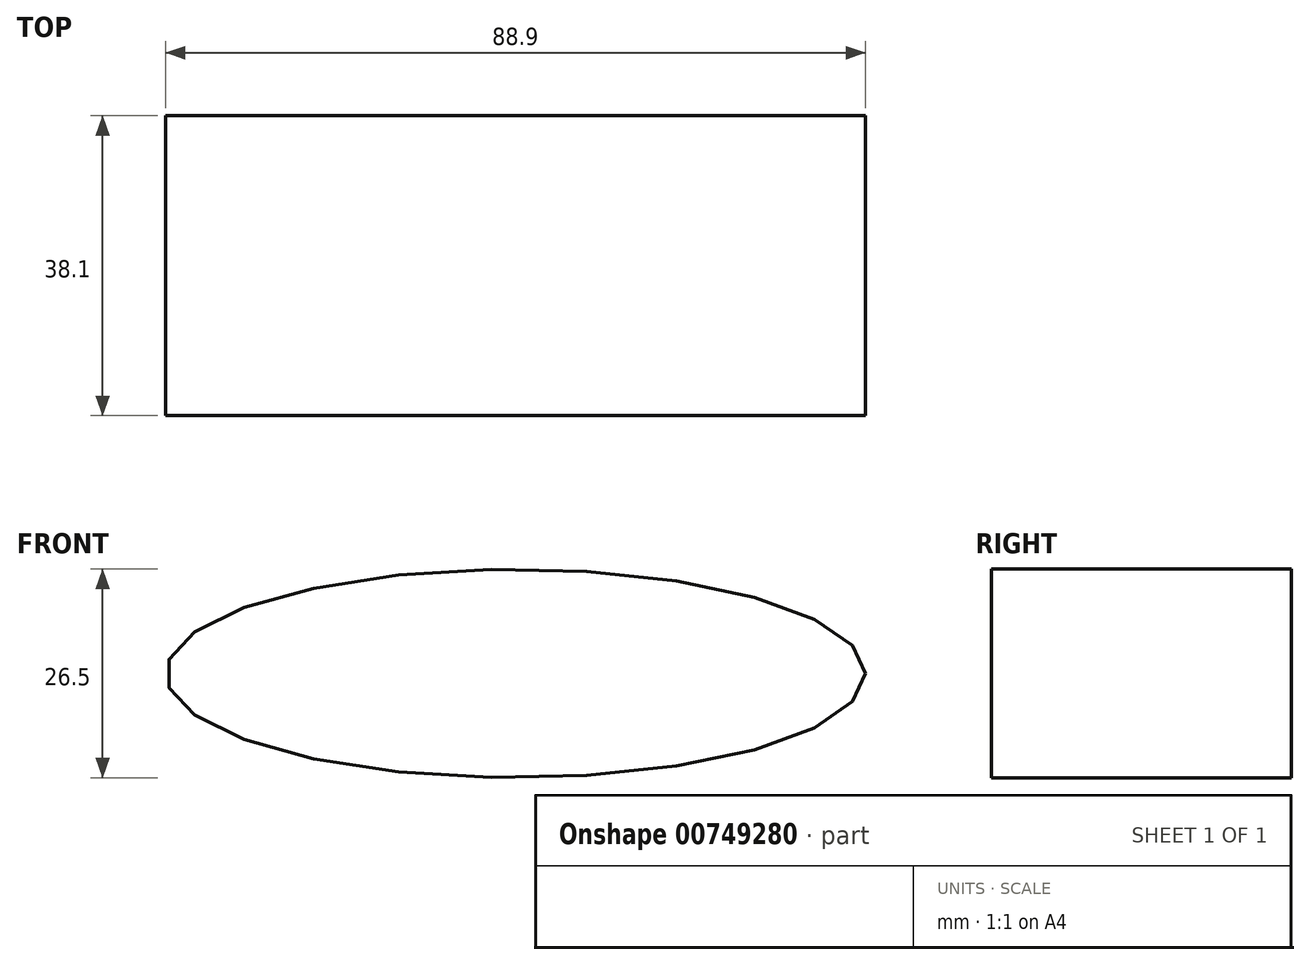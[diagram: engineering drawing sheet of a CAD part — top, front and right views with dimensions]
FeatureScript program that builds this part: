
annotation { "Feature Type Name" : "Feature", "Feature Type Description" : "" }
export const myFeature = defineFeature(function(context is Context, id is Id, definition is map)
    precondition{}
    {
        {
            var Q0;
            Q0=qCreatedBy(makeId("Front.planeOp"),FACE);
            var sketch = newSketch(context, id + "F0", { "sketchPlane" : qUnion([Q0])});
            skEllipse(sketch, "E0", {"center": v(0, 0) * mm, "majorRadius": 44.45 * mm, "minorRadius": 13.25 * mm, "majorAxis": v(1, 0)});
            skSolve(sketch);
        }
        {
            var Q0;
            Q0 = qSketchRegion(id + "F0", true);
            extrude(context, id + "F1", {"entities" : qUnion([Q0]), "depth" : 38.1 * mm, "offsetDistance" : 25.4 * mm});
        }
    });
